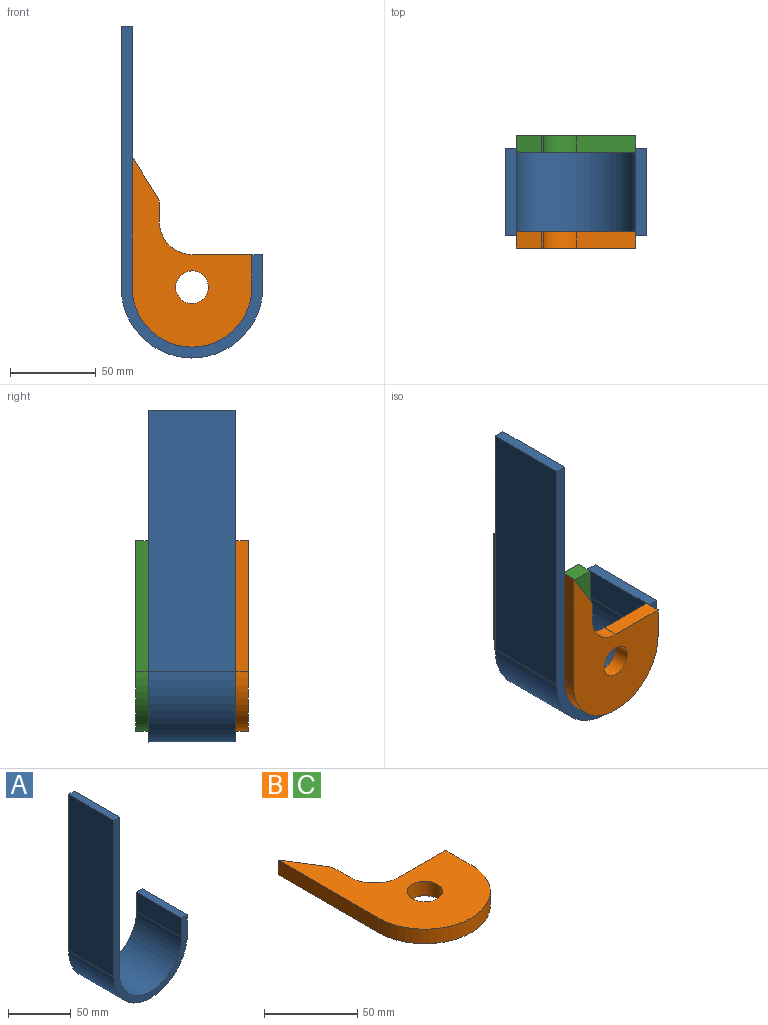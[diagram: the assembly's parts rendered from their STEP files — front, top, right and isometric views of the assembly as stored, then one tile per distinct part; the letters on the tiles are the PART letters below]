
ASSEMBLY  parts=3 mates=5
PART A: 10 faces, bbox 82.6x50.8x193.7 mm
  f0: plane 50.8x19.05mm, normal (1,0,0), area 967.7mm2, adj f1,f7,f8,f9
  f1: plane 50.8x6.35mm, normal (0,0,1), area 322.6mm2, adj f0,f2,f8,f9
  f2: plane 50.8x19.05mm, normal (-1,0,0), area 967.7mm2, adj f1,f3,f8,f9
  f3: cylinder r=34.92mm len=69.85mm, axis (0,1,0), area 5573.8mm2, adj f2,f4,f8,f9
  f4: plane 152.4x50.8mm, normal (1,0,0), area 7741.9mm2, adj f3,f5,f8,f9
  f5: plane 50.8x6.35mm, normal (0,0,1), area 322.6mm2, adj f4,f6,f8,f9
  f6: plane 152.4x50.8mm, normal (-1,0,0), area 7741.9mm2, adj f5,f7,f8,f9
  f7: cylinder r=41.27mm len=82.55mm, axis (0,1,0), area 6587.2mm2, adj f0,f6,f8,f9
  f8: plane 193.68x82.55mm, normal (0,-1,0), area 1848.8mm2, adj f0,f1,f2,f3,f4,f5,f6,f7
  f9: plane 193.68x82.55mm, normal (0,1,0), area 1848.8mm2, adj f0,f1,f2,f3,f4,f5,f6,f7
PART B: 11 faces, bbox 69.9x111.1x9.5 mm
  f0: plane 10.88x9.53mm, normal (1,0,0), area 103.6mm2, adj f1,f7,f8,f9
  f1: cylinder r=6.35mm len=9.53mm, axis (0,0,-1), area 33.8mm2, adj f0,f2,f8,f9
  f2: plane 23.86x14.91mm, normal (0.85,0.53,0), area 268mm2, adj f1,f3,f8,f9
  f3: plane 76.2x9.53mm, normal (-1,0,0), area 725.8mm2, adj f2,f4,f8,f9
  f4: cylinder r=34.92mm len=69.85mm, axis (0,0,-1), area 1045.1mm2, adj f3,f5,f8,f9
  f5: plane 19.05x9.53mm, normal (1,0,0), area 181.5mm2, adj f4,f6,f8,f9
  f6: plane 34.93x9.53mm, normal (0,1,0), area 332.7mm2, adj f5,f7,f8,f9
  f7: cylinder r=19.05mm len=19.05mm, axis (0,0,-1), area 285mm2, adj f0,f6,f8,f9
  f8: plane 111.13x69.85mm, normal (0,0,1), area 3744.8mm2, adj f0,f1,f2,f3,f4,f5,f6,f7
  f9: plane 111.13x69.85mm, normal (0,0,-1), area 3744.8mm2, adj f0,f1,f2,f3,f4,f5,f6,f7
  f10: cylinder r=9.53mm len=19.05mm, axis (0,0,1), area 570mm2, adj f8,f9
PART C: same geometry as B
PLACE A t=(-112.01,-24.74,-217.16)mm
PLACE B rot(axis=(1,0,0),90deg) t=(-70.74,-73.38,-217.16)mm
PLACE C rot(axis=(1,0,0),90deg) t=(-70.74,-17.37,-217.16)mm
MATE parallel A.f1 <-> C.f6  axis (0,0,1) through (-32.64,-50.14,-198.11)mm
MATE parallel A.f9 <-> C.f9  axis (0,1,0) through (-88.19,-24.74,-186.64)mm
MATE parallel B.f8 <-> C.f9  axis (0,-1,0) through (-89.79,-82.91,-173.62)mm
MATE cylindrical B.f4 <-> A.f3  axis (0,1,0) through (-70.74,-78.14,-217.16)mm
MATE cylindrical C.f4 <-> A.f3  axis (0,1,0) through (-70.74,-22.14,-217.16)mm
